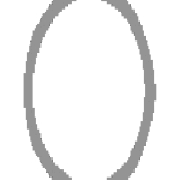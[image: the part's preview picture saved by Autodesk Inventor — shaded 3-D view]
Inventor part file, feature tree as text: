
AUTODESK INVENTOR PART (.ipt)
format: ipt  version: 2021 (Build 250183000, 183)  size: 109,568 bytes
history: native  units: in
note: dims shown in document units (in); Inventor stores cm internally (conversion verified against a paired STEP export)
features: other x4, sketch x3, plane x1
ambient origin geometry x8: Origin, YZ Plane, XZ Plane, XY Plane, X Axis, Y Axis, Z Axis, Center Point
bodies: Solid1 (feature_tree), Body (feature_tree)
feature tree (8):
  other  "Driven Length"
  other  "Frame Generator"
  other  "Start Plane"
  other  "End Plane"
  sketch  "Sketch"  dims[d2=16.0833in d4=-0.0in d5=16.0833in d6=0.12in d7=0.0in d8=90.0deg d9=16.0833in]
  sketch  "Sketch2"  dims[d0=1.0in]
  plane  "Work Plane3"
  sketch  "Sketch3"  dims[d1=0.065in]
